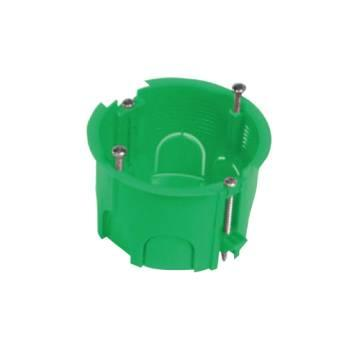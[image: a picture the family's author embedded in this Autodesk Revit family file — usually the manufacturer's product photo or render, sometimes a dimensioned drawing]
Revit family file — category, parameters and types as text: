
# Revit family: Building-ContenitoriIncasso-GEWISS-24SC-GREENWALL-SCATOLE-INCASSO_TONDE
name_source: partatom
category: Apparecchi elettrici
revit_build: Autodesk Revit 2016 (Build: 20161004_0715(x64)
units: mm (PartAtom-declared; Revit-internal decimal feet)

## family parameters
Condiviso = Sì
Host = Superficie
Mantenere orientamento annotazione = Sì
Numero OmniClass = 23.80.30.14.24
Punto di calcolo locali = Sì
Quota connettore circolare = Usa diametro
Taglio con vuoti quando caricato = Sì
Tipo di parte = Normale
Titolo OmniClass = Junction Boxes

## types (1)
- GW24234PM - Halogen free - D.65x45
    Caratteristiche = Halogen free
    Carico apparente = 0 VA
    Catalogo = BUILDING
    Catalogo Serie = 24SC
    Classificazione = Altro
    Codice EAN = 8011564802025
    Codice Electrocod = 0210
    Descrizione = SCATOLA TONDA PARETI LEGGERE GREEN
    Descrizione: = Tonda
    Dimensioni (mm) = Ã˜ 65x45
    Glow Wire Test = 850°C
    Grado di protezione = IP40
    IDF = fefa3dd4-31f8-4ed0-99b7-12ba546c9694
    IDT = d2635837-3151-40c3-856d-c8cfc8bd2e75
    Immagine tipo = GW24234PM.jpg
    Installazione = Incasso
    Interasse fissaggio supporti = 60MM
    Metallo = GEWISS - Elementi acciaio
    Modello = GW24234PM
    Per Pareti = Cartongesso
    Produttore = GEWISS S.p.A.
    Profondità = 45 mm  [stored 0.147638 ft]
    Prospetto di default = 1219.2 mm  [stored 4 ft]
    Resistenza agli urti = IK07
    SEO = Scatola
    Scatola = GEWISS - scatola a incasso
    Scheda Tecnica = https://www.gewiss.com
    Temperatura di impiego = -15 +60 °C
    Termopressione con biglia = 70 °C
    Tipo Materiale = Halogen free secondo norma EN 60754-2
    URL = https://www.gewiss.com
    Versione file RFA = 19.0
    Voltaggio = 0 V

note: [stored X ft] marks values corroborated as IEEE doubles in the binary element streams (Revit-internal decimal feet)

## geometry (parser evidence)
native form markers: Blend x2, Sweep x2
no freeform markers — native parametric forms only
